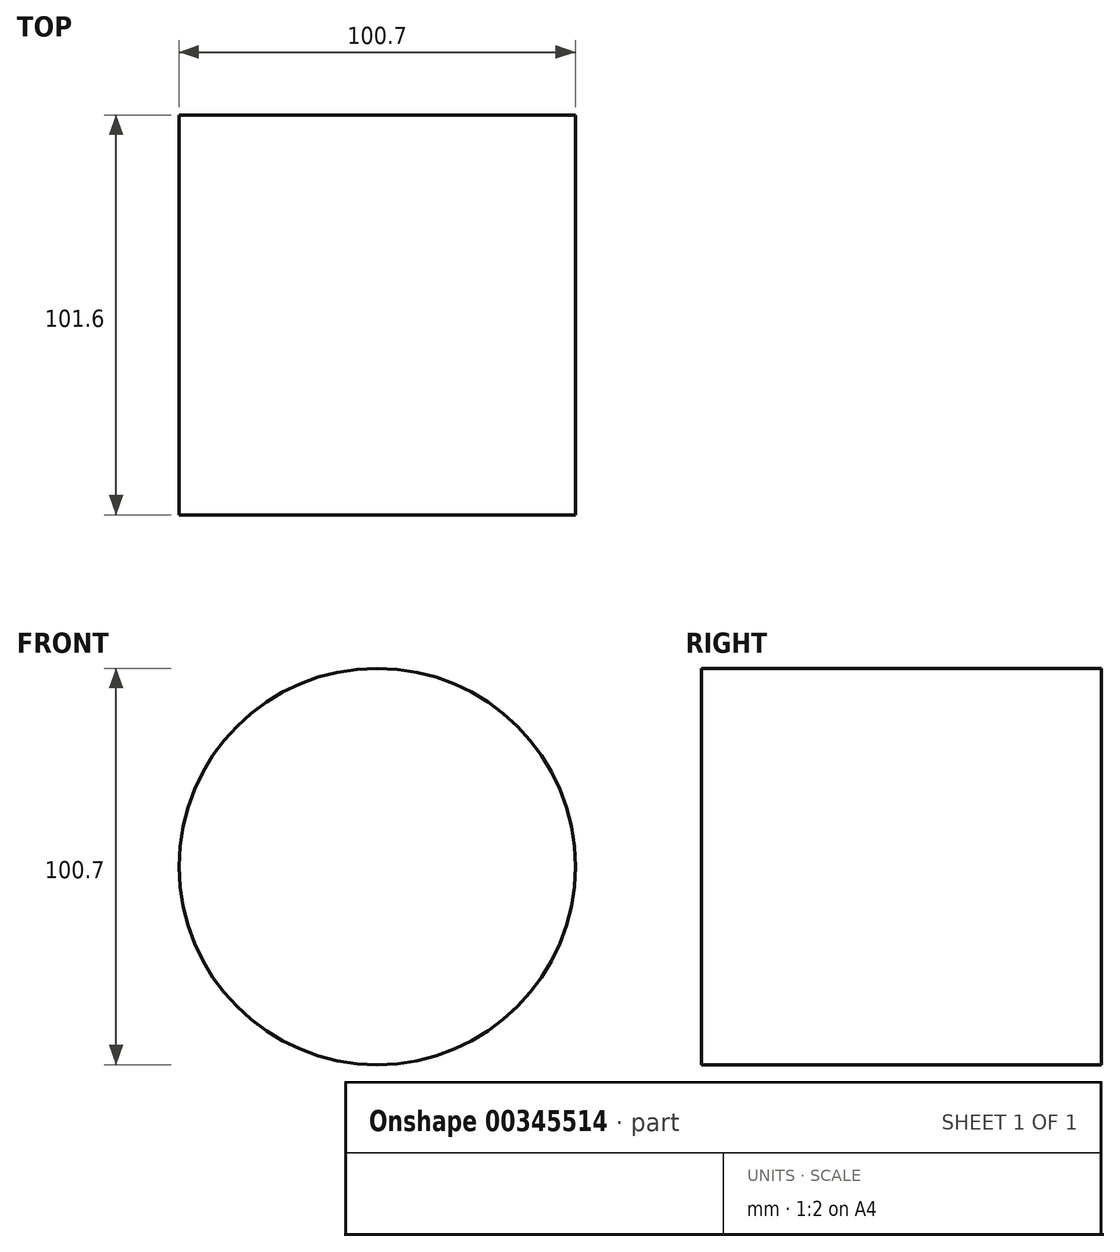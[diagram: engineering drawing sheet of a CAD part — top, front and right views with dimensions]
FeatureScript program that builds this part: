
annotation { "Feature Type Name" : "Feature", "Feature Type Description" : "" }
export const myFeature = defineFeature(function(context is Context, id is Id, definition is map)
    precondition{}
    {
        {
            var Q0;
            Q0=qCreatedBy(makeId("Front.planeOp"),FACE);
            var sketch = newSketch(context, id + "F0", { "sketchPlane" : qUnion([Q0])});
            skCircle(sketch, "E0", {"center": v(0, 0) * mm, "radius": 50.35 * mm});
            skSolve(sketch);
        }
        {
            var Q0;
            Q0 = qSketchRegion(id + "F0", true);
            extrude(context, id + "F1", {"entities" : qUnion([Q0]), "depth" : 50.8 * mm});
        }
        {
            var Q0;
            Q0=qCreatedBy(makeId("Front.planeOp"),FACE);
            var sketch = newSketch(context, id + "F2", { "sketchPlane" : qUnion([Q0])});
            skCircle(sketch, "E1.cCircle", {"center": v(0, 0) * mm, "radius": 43.4 * mm, "construction": true});
            skLineSegment(sketch, "E1.0", {"start": v(-25.06, 43.4) * mm, "end": v(25.06, 43.4) * mm});
            skLineSegment(sketch, "E1.1", {"start": v(25.06, 43.4) * mm, "end": v(50.12, 0) * mm});
            skLineSegment(sketch, "E1.2", {"start": v(50.12, 0) * mm, "end": v(25.06, -43.4) * mm});
            skLineSegment(sketch, "E1.3", {"start": v(25.06, -43.4) * mm, "end": v(-25.06, -43.4) * mm});
            skLineSegment(sketch, "E1.4", {"start": v(-25.06, -43.4) * mm, "end": v(-50.12, 0) * mm});
            skLineSegment(sketch, "E1.5", {"start": v(-50.12, 0) * mm, "end": v(-25.06, 43.4) * mm});
            skPoint(sketch, "E1.0.midPoint", {"position": v(0, 43.4) * mm});
            skLineSegment(sketch, "E2", {"start": v(-25.06, 43.4) * mm, "end": v(0, 0) * mm});
            skLineSegment(sketch, "E3", {"start": v(0, 0) * mm, "end": v(25.06, 43.4) * mm});
            skLineSegment(sketch, "E4", {"start": v(0, 0) * mm, "end": v(25.06, -43.4) * mm});
            skLineSegment(sketch, "E5", {"start": v(-50.12, 0) * mm, "end": v(50.12, 0) * mm});
            skLineSegment(sketch, "E6", {"start": v(0, 0) * mm, "end": v(-25.06, -43.4) * mm});
            skSolve(sketch);
        }
        {
            var Q0;
            Q0 = qSketchRegion(id + "F2", true);
            extrude(context, id + "F3", {"entities" : qUnion([Q0]), "operationType" : NewBodyOperationType.ADD, "depth" : 25.4 * mm});
        }
        {
            var Q0;
            Q0 = qSketchRegion(id + "F2", true);
            extrude(context, id + "F4", {"entities" : qUnion([Q0]), "operationType" : NewBodyOperationType.ADD, "depth" : 25.4 * mm});
        }
        {
            var Q0;
            Q0=makeQuery(id+"F1.opExtrude","CAP_FACE",FACE,{"disambiguationData":[OSD([sQuery(id+"F0.wireOp",EDGE,"E0")])],"isStart":false});
            extrude(context, id + "F5", {"entities" : qUnion([Q0]), "operationType" : NewBodyOperationType.ADD, "depth" : 50.8 * mm});
        }
    });
